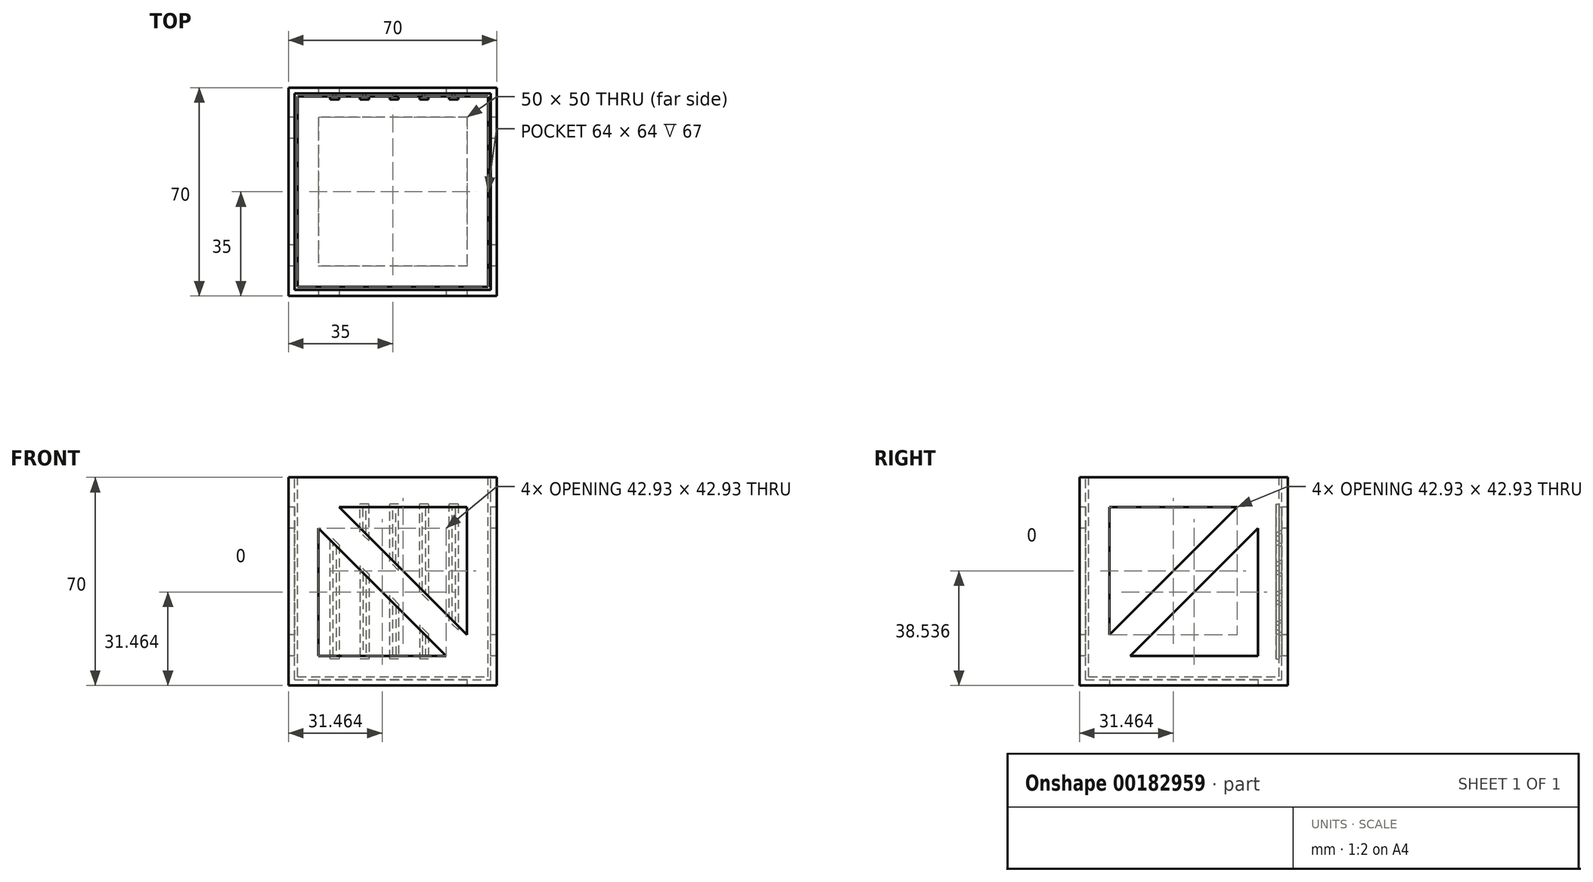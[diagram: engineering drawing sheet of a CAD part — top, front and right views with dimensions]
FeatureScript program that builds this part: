
annotation { "Feature Type Name" : "Feature", "Feature Type Description" : "" }
export const myFeature = defineFeature(function(context is Context, id is Id, definition is map)
    precondition{}
    {
        {
            var Q0;
            Q0=qCreatedBy(makeId("Top.planeOp"),FACE);
            var sketch = newSketch(context, id + "F0", { "sketchPlane" : qUnion([Q0])});
            skLineSegment(sketch, "E0.bottom", {"start": v(35, 35) * mm, "end": v(-35, 35) * mm});
            skLineSegment(sketch, "E0.top", {"start": v(35, -35) * mm, "end": v(-35, -35) * mm});
            skLineSegment(sketch, "E0.left", {"start": v(35, 35) * mm, "end": v(35, -35) * mm});
            skLineSegment(sketch, "E0.right", {"start": v(-35, 35) * mm, "end": v(-35, -35) * mm});
            skPoint(sketch, "E0.middle", {"position": v(0, 0) * mm});
            skLineSegment(sketch, "E1.0", {"start": v(25, 25) * mm, "end": v(-25, 25) * mm});
            skLineSegment(sketch, "E1.1", {"start": v(25, 25) * mm, "end": v(25, -25) * mm});
            skLineSegment(sketch, "E1.2", {"start": v(25, -25) * mm, "end": v(-25, -25) * mm});
            skLineSegment(sketch, "E1.3", {"start": v(-25, 25) * mm, "end": v(-25, -25) * mm});
            skLineSegment(sketch, "E2.0", {"start": v(33, 33) * mm, "end": v(-33, 33) * mm});
            skLineSegment(sketch, "E2.1", {"start": v(33, 33) * mm, "end": v(33, -33) * mm});
            skLineSegment(sketch, "E2.2", {"start": v(33, -33) * mm, "end": v(-33, -33) * mm});
            skLineSegment(sketch, "E2.3", {"start": v(-33, 33) * mm, "end": v(-33, -33) * mm});
            skSolve(sketch);
        }
        {
            var Q0;
            Q0=makeQuery(id+"F0.imprint","IMPRINT",FACE,{"disambiguationData":[TD([[makeQuery(id+"F0.imprint","IMPRINT",EDGE,{"derivedFrom":sQuery(id+"F0.wireOp",EDGE,"E1.0")}),-1.0]])]});
            extrude(context, id + "F1", {"entities" : qUnion([Q0]), "depth" : 2 * mm});
        }
        {
            var Q0;
            Q0=makeQuery(id+"F0.imprint","IMPRINT",FACE,{"disambiguationData":[TD([[makeQuery(id+"F0.imprint","IMPRINT",EDGE,{"derivedFrom":sQuery(id+"F0.wireOp",EDGE,"E0.bottom")}),1.0]])]});
            extrude(context, id + "F2", {"entities" : qUnion([Q0]), "operationType" : NewBodyOperationType.ADD, "depth" : 70 * mm});
        }
        {
            var Q0;
            Q0=makeQuery(id+"F2.opExtrude","SWEPT_FACE",FACE,{"disambiguationData":[OSD([sQuery(id+"F0.wireOp",EDGE,"E0.top")])]});
            var sketch = newSketch(context, id + "F3", { "sketchPlane" : qUnion([Q0])});
            skLineSegment(sketch, "E3.0", {"start": v(35, 0) * mm, "end": v(-35, 0) * mm});
            skLineSegment(sketch, "E4.0", {"start": v(35, 70) * mm, "end": v(35, 0) * mm});
            skLineSegment(sketch, "E5.0", {"start": v(-35, 70) * mm, "end": v(-35, 0) * mm});
            skLineSegment(sketch, "E6.0", {"start": v(35, 70) * mm, "end": v(-35, 70) * mm});
            skLineSegment(sketch, "E7.0", {"start": v(25, 10) * mm, "end": v(-25, 10) * mm});
            skLineSegment(sketch, "E7.1", {"start": v(25, 60) * mm, "end": v(25, 10) * mm});
            skLineSegment(sketch, "E7.2", {"start": v(25, 60) * mm, "end": v(-25, 60) * mm});
            skLineSegment(sketch, "E7.3", {"start": v(-25, 60) * mm, "end": v(-25, 10) * mm});
            skLineSegment(sketch, "E8", {"start": v(35, 0) * mm, "end": v(-35, 70) * mm, "construction": true});
            skLineSegment(sketch, "E9.0", {"start": v(17.93, 10) * mm, "end": v(-25, 52.93) * mm});
            skLineSegment(sketch, "E10.trimOffspring", {"start": v(25, 17.07) * mm, "end": v(-17.93, 60) * mm});
            skSolve(sketch);
        }
        {
            var Q0;
            {var subQ3=sQuery(id+"F3.wireOp",EDGE,"E10.trimOffspring");Q0=makeQuery(id+"F3.imprint","IMPRINT",FACE,{"disambiguationData":[TD([[makeQuery(id+"F3.imprint","IMPRINT",EDGE,{"derivedFrom":subQ3}),-1.0]])]});}
            var Q1;
            {var subQ3=sQuery(id+"F3.wireOp",EDGE,"E9.0");Q1=makeQuery(id+"F3.imprint","IMPRINT",FACE,{"disambiguationData":[TD([[makeQuery(id+"F3.imprint","IMPRINT",EDGE,{"derivedFrom":subQ3}),1.0]])]});}
            extrude(context, id + "F4", {"entities" : qUnion([Q0, Q1]), "operationType" : NewBodyOperationType.REMOVE, "endBound" : BoundingType.THROUGH_ALL, "oppositeDirection" : true, "depth" : 25 * mm});
        }
        {
            var Q0;
            Q0=makeQuery(id+"F2.opExtrude","SWEPT_FACE",FACE,{"disambiguationData":[OSD([sQuery(id+"F0.wireOp",EDGE,"E0.right")])]});
            var sketch = newSketch(context, id + "F5", { "sketchPlane" : qUnion([Q0])});
            skLineSegment(sketch, "E11.0", {"start": v(35, 0) * mm, "end": v(-35, 0) * mm});
            skLineSegment(sketch, "E12.0", {"start": v(35, 70) * mm, "end": v(35, 0) * mm});
            skLineSegment(sketch, "E13.0", {"start": v(-35, 70) * mm, "end": v(-35, 0) * mm});
            skLineSegment(sketch, "E14.0", {"start": v(35, 70) * mm, "end": v(-35, 70) * mm});
            skLineSegment(sketch, "E15.0", {"start": v(25, 10) * mm, "end": v(-25, 10) * mm});
            skLineSegment(sketch, "E15.1", {"start": v(25, 60) * mm, "end": v(25, 10) * mm});
            skLineSegment(sketch, "E15.2", {"start": v(25, 60) * mm, "end": v(-25, 60) * mm});
            skLineSegment(sketch, "E15.3", {"start": v(-25, 60) * mm, "end": v(-25, 10) * mm});
            skLineSegment(sketch, "E16", {"start": v(35, 0) * mm, "end": v(-35, 70) * mm, "construction": true});
            skLineSegment(sketch, "E17.0", {"start": v(17.93, 10) * mm, "end": v(-25, 52.93) * mm});
            skLineSegment(sketch, "E18.trimOffspring", {"start": v(25, 17.07) * mm, "end": v(-17.93, 60) * mm});
            skSolve(sketch);
        }
        {
            var Q0;
            {var subQ3=sQuery(id+"F5.wireOp",EDGE,"E18.trimOffspring");Q0=makeQuery(id+"F5.imprint","IMPRINT",FACE,{"disambiguationData":[TD([[makeQuery(id+"F5.imprint","IMPRINT",EDGE,{"derivedFrom":subQ3}),-1.0]])]});}
            var Q1;
            {var subQ3=sQuery(id+"F5.wireOp",EDGE,"E17.0");Q1=makeQuery(id+"F5.imprint","IMPRINT",FACE,{"disambiguationData":[TD([[makeQuery(id+"F5.imprint","IMPRINT",EDGE,{"derivedFrom":subQ3}),1.0]])]});}
            extrude(context, id + "F6", {"entities" : qUnion([Q0, Q1]), "operationType" : NewBodyOperationType.REMOVE, "endBound" : BoundingType.THROUGH_ALL, "oppositeDirection" : true, "depth" : 25 * mm});
        }
        {
            var Q0;
            Q0=makeQuery(id+"F2.opExtrude","CAP_FACE",FACE,{"disambiguationData":[OSD([sQuery(id+"F0.wireOp",EDGE,"E0.bottom"),sQuery(id+"F0.wireOp",EDGE,"E0.top"),sQuery(id+"F0.wireOp",EDGE,"E0.left"),sQuery(id+"F0.wireOp",EDGE,"E0.right"),sQuery(id+"F0.wireOp",EDGE,"E2.0"),sQuery(id+"F0.wireOp",EDGE,"E2.1"),sQuery(id+"F0.wireOp",EDGE,"E2.2"),sQuery(id+"F0.wireOp",EDGE,"E2.3")])],"isStart":false});
            var sketch = newSketch(context, id + "F7", { "sketchPlane" : qUnion([Q0])});
            skLineSegment(sketch, "E19.0", {"start": v(33, 33) * mm, "end": v(-33, 33) * mm});
            skLineSegment(sketch, "E20.0", {"start": v(-33, 33) * mm, "end": v(-33, -33) * mm});
            skLineSegment(sketch, "E21.0", {"start": v(33, 33) * mm, "end": v(33, -33) * mm});
            skLineSegment(sketch, "E22.0", {"start": v(33, -33) * mm, "end": v(-33, -33) * mm});
            skSolve(sketch);
        }
        {
            var Q0;
            Q0=makeQuery(id+"F7.imprint","IMPRINT",FACE,{"disambiguationData":[TD([[makeQuery(id+"F7.imprint","IMPRINT",EDGE,{"derivedFrom":sQuery(id+"F7.wireOp",EDGE,"E19.0")}),1.0]])]});
            var Q1;
            Q1=makeQuery(id+"F1.opExtrude","CAP_FACE",FACE,{"disambiguationData":[OSD([sQuery(id+"F0.wireOp",EDGE,"E1.0"),sQuery(id+"F0.wireOp",EDGE,"E1.1"),sQuery(id+"F0.wireOp",EDGE,"E1.2"),sQuery(id+"F0.wireOp",EDGE,"E1.3"),sQuery(id+"F0.wireOp",EDGE,"E2.0"),sQuery(id+"F0.wireOp",EDGE,"E2.1"),sQuery(id+"F0.wireOp",EDGE,"E2.2"),sQuery(id+"F0.wireOp",EDGE,"E2.3")])],"isStart":false});
            extrude(context, id + "F8", {"entities" : qUnion([Q0]), "endBound" : BoundingType.UP_TO_SURFACE, "oppositeDirection" : true, "endBoundEntityFace" : qUnion([Q1]), "depth" : 25 * mm});
        }
        {
            var Q0;
            Q0=makeQuery(id+"F8.opExtrude","SWEPT_FACE",FACE,{"disambiguationData":[OSD([sQuery(id+"F7.wireOp",EDGE,"E19.0")])]});
            var sketch = newSketch(context, id + "F9", { "sketchPlane" : qUnion([Q0])});
            skLineSegment(sketch, "E23", {"start": v(0, 2) * mm, "end": v(0, 70) * mm, "construction": true});
            skLineSegment(sketch, "E24", {"start": v(-10, 70) * mm, "end": v(-10, 2) * mm, "construction": true});
            skLineSegment(sketch, "E25", {"start": v(-20, 2) * mm, "end": v(-20, 70) * mm, "construction": true});
            skLineSegment(sketch, "E26", {"start": v(-30, 2) * mm, "end": v(-30, 70) * mm, "construction": true});
            skLineSegment(sketch, "E27.1.0.0", {"start": v(30, 2) * mm, "end": v(30, 70) * mm, "construction": true});
            skLineSegment(sketch, "E27.1.0.1", {"start": v(20, 70) * mm, "end": v(20, 2) * mm, "construction": true});
            skLineSegment(sketch, "E27.direction1", {"start": v(-10, 2) * mm, "end": v(20, 2) * mm, "construction": true});
            skLineSegment(sketch, "E28", {"start": v(10, 2) * mm, "end": v(10, 70) * mm, "construction": true});
            skLineSegment(sketch, "E29.0", {"start": v(-17.93, 10) * mm, "end": v(25, 52.93) * mm});
            skLineSegment(sketch, "E30.0", {"start": v(25, 52.93) * mm, "end": v(25, 10) * mm});
            skLineSegment(sketch, "E31.0", {"start": v(-17.93, 10) * mm, "end": v(25, 10) * mm});
            skLineSegment(sketch, "E32.0", {"start": v(-25, 17.07) * mm, "end": v(17.93, 60) * mm});
            skLineSegment(sketch, "E33.0", {"start": v(-25, 60) * mm, "end": v(-25, 17.07) * mm});
            skLineSegment(sketch, "E34.0", {"start": v(-25, 60) * mm, "end": v(17.93, 60) * mm});
            skLineSegment(sketch, "E35", {"start": v(-10, 32.07) * mm, "end": v(-10, 60) * mm});
            skLineSegment(sketch, "E36", {"start": v(-10, 60) * mm, "end": v(-11, 60) * mm});
            skLineSegment(sketch, "E37", {"start": v(-11, 60) * mm, "end": v(-11, 31.07) * mm});
            skLineSegment(sketch, "E38", {"start": v(0, 42.07) * mm, "end": v(0, 60) * mm});
            skLineSegment(sketch, "E39", {"start": v(-1, 41.07) * mm, "end": v(-1, 60) * mm});
            skLineSegment(sketch, "E40", {"start": v(10, 52.07) * mm, "end": v(10, 60) * mm});
            skLineSegment(sketch, "E41", {"start": v(9, 51.07) * mm, "end": v(9, 60) * mm});
            skLineSegment(sketch, "E42", {"start": v(-20, 22.07) * mm, "end": v(-20, 60) * mm});
            skLineSegment(sketch, "E43", {"start": v(-21, 60) * mm, "end": v(-21, 21.07) * mm});
            skLineSegment(sketch, "E44", {"start": v(-10, 17.93) * mm, "end": v(-10, 10) * mm});
            skLineSegment(sketch, "E45", {"start": v(-11, 16.93) * mm, "end": v(-11, 10) * mm});
            skLineSegment(sketch, "E46", {"start": v(-1, 26.93) * mm, "end": v(-1, 10) * mm});
            skLineSegment(sketch, "E47", {"start": v(0, 10) * mm, "end": v(0, 27.93) * mm});
            skLineSegment(sketch, "E48", {"start": v(10, 37.93) * mm, "end": v(10, 10) * mm});
            skLineSegment(sketch, "E49", {"start": v(9, 36.93) * mm, "end": v(9, 10) * mm});
            skLineSegment(sketch, "E50", {"start": v(20, 10) * mm, "end": v(20, 47.93) * mm});
            skLineSegment(sketch, "E51", {"start": v(19, 46.93) * mm, "end": v(19, 10) * mm});
            skSolve(sketch);
        }
        {
            var Q0;
            {var subQ0=sQuery(id+"F9.wireOp",EDGE,"E35");Q0=makeQuery(id+"F9.imprint","IMPRINT",FACE,{"disambiguationData":[TD([[makeQuery(id+"F9.imprint","IMPRINT",EDGE,{"derivedFrom":subQ0}),1.0]])]});}
            extrude(context, id + "F10", {"entities" : qUnion([Q0]), "operationType" : NewBodyOperationType.REMOVE, "oppositeDirection" : true, "depth" : 1 * mm});
        }
        {
            var Q0;
            {var subQ0=sQuery(id+"F9.wireOp",EDGE,"E42");Q0=makeQuery(id+"F9.imprint","IMPRINT",FACE,{"disambiguationData":[TD([[makeQuery(id+"F9.imprint","IMPRINT",EDGE,{"derivedFrom":subQ0}),1.0]])]});}
            var Q1;
            {var subQ0=sQuery(id+"F9.wireOp",EDGE,"E38");Q1=makeQuery(id+"F9.imprint","IMPRINT",FACE,{"disambiguationData":[TD([[makeQuery(id+"F9.imprint","IMPRINT",EDGE,{"derivedFrom":subQ0}),1.0]])]});}
            var Q2;
            {var subQ0=sQuery(id+"F9.wireOp",EDGE,"E40");Q2=makeQuery(id+"F9.imprint","IMPRINT",FACE,{"disambiguationData":[TD([[makeQuery(id+"F9.imprint","IMPRINT",EDGE,{"derivedFrom":subQ0}),1.0]])]});}
            var Q3;
            {var subQ0=sQuery(id+"F9.wireOp",EDGE,"E50");Q3=makeQuery(id+"F9.imprint","IMPRINT",FACE,{"disambiguationData":[TD([[makeQuery(id+"F9.imprint","IMPRINT",EDGE,{"derivedFrom":subQ0}),1.0]])]});}
            var Q4;
            {var subQ0=sQuery(id+"F9.wireOp",EDGE,"E48");Q4=makeQuery(id+"F9.imprint","IMPRINT",FACE,{"disambiguationData":[TD([[makeQuery(id+"F9.imprint","IMPRINT",EDGE,{"derivedFrom":subQ0}),-1.0]])]});}
            var Q5;
            {var subQ0=sQuery(id+"F9.wireOp",EDGE,"E46");Q5=makeQuery(id+"F9.imprint","IMPRINT",FACE,{"disambiguationData":[TD([[makeQuery(id+"F9.imprint","IMPRINT",EDGE,{"derivedFrom":subQ0}),1.0]])]});}
            var Q6;
            {var subQ0=sQuery(id+"F9.wireOp",EDGE,"E44");Q6=makeQuery(id+"F9.imprint","IMPRINT",FACE,{"disambiguationData":[TD([[makeQuery(id+"F9.imprint","IMPRINT",EDGE,{"derivedFrom":subQ0}),-1.0]])]});}
            extrude(context, id + "F11", {"entities" : qUnion([Q0, Q1, Q2, Q3, Q4, Q5, Q6]), "operationType" : NewBodyOperationType.REMOVE, "oppositeDirection" : true, "depth" : 1 * mm});
        }
        {
            var Q0;
            Q0=makeQuery(id+"F8.opExtrude","CAP_FACE",FACE,{"disambiguationData":[OSD([sQuery(id+"F7.wireOp",EDGE,"E19.0"),sQuery(id+"F7.wireOp",EDGE,"E20.0"),sQuery(id+"F7.wireOp",EDGE,"E21.0"),sQuery(id+"F7.wireOp",EDGE,"E22.0")])],"isStart":true});
            var Q1;
            Q1=makeQuery(id+"F8.opExtrude","SWEPT_BODY",BODY,{"disambiguationData":[OSD([sQuery(id+"F7.wireOp",EDGE,"E19.0"),sQuery(id+"F7.wireOp",EDGE,"E20.0"),sQuery(id+"F7.wireOp",EDGE,"E21.0"),sQuery(id+"F7.wireOp",EDGE,"E22.0")])]});
            shell(context, id + "F12", {"entities" : qUnion([Q0]), "parts" : qUnion([Q1]), "thickness" : 1 * mm});
        }
    });
